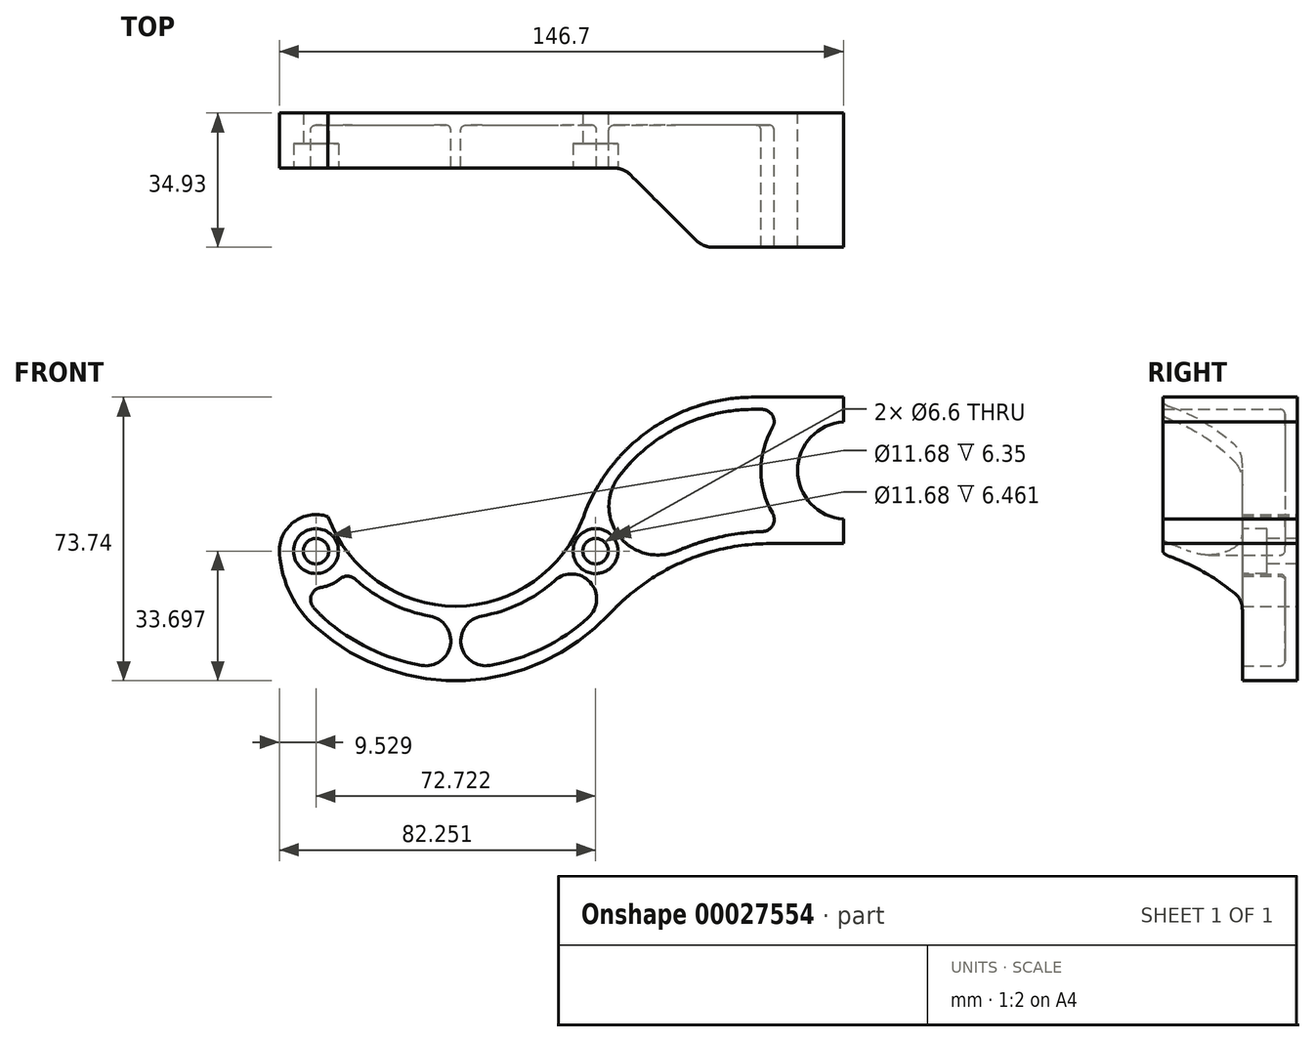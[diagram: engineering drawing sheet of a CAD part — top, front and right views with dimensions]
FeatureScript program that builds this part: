
annotation { "Feature Type Name" : "Feature", "Feature Type Description" : "" }
export const myFeature = defineFeature(function(context is Context, id is Id, definition is map)
    precondition{}
    {
        {
            var Q0;
            Q0=qCreatedBy(makeId("Front.planeOp"),FACE);
            var sketch = newSketch(context, id + "F0", { "sketchPlane" : qUnion([Q0])});
            skCircle(sketch, "E0", {"center": v(0, 0) * mm, "radius": 34.05 * mm, "construction": true});
            skLineSegment(sketch, "E1", {"start": v(0, 0) * mm, "end": v(-36.36, -21) * mm, "construction": true});
            skLineSegment(sketch, "E2", {"start": v(0, 0) * mm, "end": v(36.36, -21) * mm, "construction": true});
            skCircle(sketch, "E3.0", {"center": v(0, 0) * mm, "radius": 41.99 * mm, "construction": true});
            skCircle(sketch, "E4", {"center": v(-36.36, -21) * mm, "radius": 7.94 * mm, "construction": true});
            skCircle(sketch, "E5", {"center": v(36.36, -21) * mm, "radius": 7.94 * mm, "construction": true});
            skArc(sketch, "E6", {"start": v(-33.22, -12) * mm, "mid": v(-42.18, -13.45) * mm, "end": v(-45.86, -21.75) * mm});
            skArc(sketch, "E7.0", {"start": v(-33.22, -12) * mm, "mid": v(0, -35.32) * mm, "end": v(33.22, -12) * mm});
            skArc(sketch, "E8", {"start": v(100.8, 12.68) * mm, "mid": v(88.9, 0) * mm, "end": v(100.8, -12.68) * mm});
            skLineSegment(sketch, "E9", {"start": v(101.6, 19.05) * mm, "end": v(101.6, -19.05) * mm, "construction": true});
            skLineSegment(sketch, "E10", {"start": v(100.8, 19.05) * mm, "end": v(100.8, 12.68) * mm});
            skLineSegment(sketch, "E11.trimOffspring", {"start": v(100.8, -12.68) * mm, "end": v(100.8, -19.05) * mm});
            skLineSegment(sketch, "E12", {"start": v(100.8, 19.05) * mm, "end": v(77.45, 19.05) * mm});
            skArc(sketch, "E13", {"start": v(77.45, 19.05) * mm, "mid": v(50.43, 10.51) * mm, "end": v(33.22, -12) * mm});
            skArc(sketch, "E14.0", {"start": v(-36.36, -40.85) * mm, "mid": v(2.59, -54.62) * mm, "end": v(40.06, -37.22) * mm});
            skLineSegment(sketch, "E15", {"start": v(100.8, -19.05) * mm, "end": v(81.76, -19.05) * mm});
            skArc(sketch, "E16", {"start": v(81.76, -19.05) * mm, "mid": v(59.01, -23.8) * mm, "end": v(40.06, -37.22) * mm});
            skArc(sketch, "E17", {"start": v(-45.86, -21.75) * mm, "mid": v(-42.96, -32.22) * mm, "end": v(-36.36, -40.85) * mm});
            skLineSegment(sketch, "E18", {"start": v(-36.36, -21) * mm, "end": v(-36.36, -40.85) * mm, "construction": true});
            skLineSegment(sketch, "E19", {"start": v(-33.22, -12) * mm, "end": v(33.22, -12) * mm, "construction": true});
            skSolve(sketch);
        }
        {
            var Q0;
            Q0 = qSketchRegion(id + "F0", true);
            extrude(context, id + "F1", {"entities" : qUnion([Q0]), "depth" : 34.92 * mm});
        }
        {
            var Q0;
            Q0=makeQuery(id+"F1.opExtrude","SWEPT_FACE",FACE,{"disambiguationData":[OSD([sQuery(id+"F0.wireOp",EDGE,"E12")])]});
            var sketch = newSketch(context, id + "F2", { "sketchPlane" : qUnion([Q0])});
            skLineSegment(sketch, "E20", {"start": v(41.03, -14.29) * mm, "end": v(-45.89, -14.29) * mm});
            skLineSegment(sketch, "E21", {"start": v(-45.89, -34.93) * mm, "end": v(-45.89, -14.29) * mm});
            skLineSegment(sketch, "E22", {"start": v(43.66, -14.29) * mm, "end": v(43.66, -44.84) * mm, "construction": true});
            skLineSegment(sketch, "E23", {"start": v(45.52, -16.15) * mm, "end": v(62.43, -33.07) * mm});
            skLineSegment(sketch, "E24", {"start": v(66.92, -34.93) * mm, "end": v(100.8, -34.93) * mm});
            skLineSegment(sketch, "E25", {"start": v(100.8, -34.93) * mm, "end": v(100.8, -38.1) * mm});
            skLineSegment(sketch, "E26", {"start": v(100.8, -38.1) * mm, "end": v(-45.89, -38.1) * mm});
            skLineSegment(sketch, "E27", {"start": v(-45.89, -38.1) * mm, "end": v(-45.89, -34.93) * mm});
            skPoint(sketch, "E28.visualSharp", {"position": v(43.66, -14.29) * mm});
            skArc(sketch, "E28.filletArc", {"start": v(45.52, -16.15) * mm, "mid": v(43.46, -14.77) * mm, "end": v(41.03, -14.29) * mm});
            skPoint(sketch, "E29.visualSharp", {"position": v(64.3, -34.92) * mm});
            skArc(sketch, "E29.filletArc", {"start": v(62.43, -33.07) * mm, "mid": v(64.5, -34.44) * mm, "end": v(66.92, -34.93) * mm});
            skSolve(sketch);
        }
        {
            var Q0;
            Q0 = qSketchRegion(id + "F2", true);
            extrude(context, id + "F3", {"entities" : qUnion([Q0]), "operationType" : NewBodyOperationType.REMOVE, "endBound" : BoundingType.THROUGH_ALL, "oppositeDirection" : true, "depth" : 25.4 * mm});
        }
        {
            var Q0;
            Q0=qCreatedBy(makeId("Front.planeOp"),FACE);
            cPlane(context, id + "F4", {"entities" : qUnion([Q0]), "cplaneType" : CPlaneType.OFFSET, "offset" : 3.17 * mm, "width" : 152.4 * mm, "height" : 152.4 * mm});
        }
        {
            var Q0;
            Q0=qCreatedBy(id+"F4.planeOp",FACE);
            var sketch = newSketch(context, id + "F5", { "sketchPlane" : qUnion([Q0])});
            skArc(sketch, "E30.0", {"start": v(-26.03, -28.36) * mm, "mid": v(-17.04, -34.52) * mm, "end": v(-6.68, -37.9) * mm});
            skArc(sketch, "E31.0", {"start": v(-34.25, -38.48) * mm, "mid": v(-22.45, -46.36) * mm, "end": v(-8.94, -50.73) * mm});
            skArc(sketch, "E32", {"start": v(-35.02, -30.42) * mm, "mid": v(-32.47, -29.69) * mm, "end": v(-30.22, -28.27) * mm});
            skArc(sketch, "E33.0", {"start": v(-37.03, -35.58) * mm, "mid": v(-35.7, -37.08) * mm, "end": v(-34.25, -38.48) * mm});
            skArc(sketch, "E34.filletArc", {"start": v(-26.03, -28.36) * mm, "mid": v(-28.1, -27.53) * mm, "end": v(-30.22, -28.27) * mm});
            skArc(sketch, "E35.filletArc", {"start": v(-35.02, -30.42) * mm, "mid": v(-37.53, -32.41) * mm, "end": v(-37.03, -35.58) * mm});
            skLineSegment(sketch, "E36", {"start": v(0, 0) * mm, "end": v(-11.59, -65.71) * mm, "construction": true});
            skLineSegment(sketch, "E37", {"start": v(0, 0) * mm, "end": v(11.66, -66.14) * mm, "construction": true});
            skArc(sketch, "E38", {"start": v(-8.94, -50.73) * mm, "mid": v(-1.4, -45.45) * mm, "end": v(-6.68, -37.9) * mm});
            skArc(sketch, "E39", {"start": v(6.68, -37.9) * mm, "mid": v(1.4, -45.45) * mm, "end": v(8.94, -50.73) * mm});
            skLineSegment(sketch, "E40", {"start": v(0, 0) * mm, "end": v(47.81, -53.1) * mm, "construction": true});
            skArc(sketch, "E41", {"start": v(34.47, -38.28) * mm, "mid": v(34.95, -29.09) * mm, "end": v(25.76, -28.6) * mm});
            skArc(sketch, "E42.trimOffspring", {"start": v(6.68, -37.9) * mm, "mid": v(16.87, -34.6) * mm, "end": v(25.76, -28.6) * mm});
            skArc(sketch, "E43.trimOffspring", {"start": v(8.94, -50.73) * mm, "mid": v(22.58, -46.3) * mm, "end": v(34.47, -38.28) * mm});
            skArc(sketch, "E44.0", {"start": v(77.45, 15.87) * mm, "mid": v(57.79, 11.22) * mm, "end": v(42.3, -1.76) * mm});
            skArc(sketch, "E45.0", {"start": v(79.73, -15.9) * mm, "mid": v(68.43, -17.37) * mm, "end": v(57.61, -20.94) * mm});
            skArc(sketch, "E46.0", {"start": v(82.35, 11.11) * mm, "mid": v(79.38, -0.02) * mm, "end": v(82.37, -11.14) * mm});
            skLineSegment(sketch, "E47.0", {"start": v(79.6, 15.87) * mm, "end": v(72.44, 15.87) * mm});
            skArc(sketch, "E48.filletArc", {"start": v(79.73, -15.9) * mm, "mid": v(82.4, -14.27) * mm, "end": v(82.37, -11.14) * mm});
            skArc(sketch, "E49.filletArc", {"start": v(82.35, 11.11) * mm, "mid": v(82.35, 14.29) * mm, "end": v(79.6, 15.87) * mm});
            skLineSegment(sketch, "E50", {"start": v(81.76, -75.96) * mm, "end": v(33.25, 15.26) * mm, "construction": true});
            skLineSegment(sketch, "E51", {"start": v(81.76, -75.96) * mm, "end": v(81.76, 37.95) * mm, "construction": true});
            skArc(sketch, "E52", {"start": v(42.3, -1.76) * mm, "mid": v(42.58, -17.23) * mm, "end": v(57.61, -20.94) * mm});
            skSolve(sketch);
        }
        {
            var Q0;
            Q0 = qSketchRegion(id + "F5", true);
            extrude(context, id + "F6", {"entities" : qUnion([Q0]), "operationType" : NewBodyOperationType.REMOVE, "depth" : 38.1 * mm});
        }
        {
            var Q0;
            Q0=makeQuery(id+"F6.boolean.opBoolean","COPY",EDGE,{"derivedFrom":makeQuery(id+"F6.opExtrude","CAP_EDGE",EDGE,{"disambiguationData":[OSD([sQuery(id+"F5.wireOp",EDGE,"E30.0")])],"isStart":true})});
            var Q1;
            Q1=makeQuery(id+"F6.boolean.opBoolean","COPY",EDGE,{"derivedFrom":makeQuery(id+"F6.opExtrude","CAP_EDGE",EDGE,{"disambiguationData":[OSD([sQuery(id+"F5.wireOp",EDGE,"E42.trimOffspring")])],"isStart":true})});
            var Q2;
            Q2=makeQuery(id+"F6.boolean.opBoolean","COPY",EDGE,{"derivedFrom":makeQuery(id+"F6.opExtrude","CAP_EDGE",EDGE,{"disambiguationData":[OSD([sQuery(id+"F5.wireOp",EDGE,"E44.0")])],"isStart":true})});
            fillet(context, id + "F7", {"entities" : qUnion([Q0, Q1, Q2]), "radius" : 1.27 * mm, "tangentPropagation" : true, "allowEdgeOverflow" : false});
        }
        {
            var Q0;
            Q0=makeQuery(id+"F3.boolean.opBoolean","COPY",FACE,{"derivedFrom":makeQuery(id+"F3.opExtrude","SWEPT_FACE",FACE,{"disambiguationData":[OSD([sQuery(id+"F2.wireOp",EDGE,"E20")])]})});
            var sketch = newSketch(context, id + "F8", { "sketchPlane" : qUnion([Q0])});
            skCircle(sketch, "E53", {"center": v(-36.36, -21) * mm, "radius": 3.3 * mm});
            skCircle(sketch, "E54", {"center": v(36.36, -21) * mm, "radius": 3.3 * mm});
            skSolve(sketch);
        }
        {
            var Q0;
            Q0 = qSketchRegion(id + "F8", true);
            extrude(context, id + "F9", {"entities" : qUnion([Q0]), "operationType" : NewBodyOperationType.REMOVE, "endBound" : BoundingType.THROUGH_ALL, "oppositeDirection" : true, "depth" : 25.4 * mm});
        }
        {
            var Q0;
            Q0=makeQuery(id+"F3.boolean.opBoolean","COPY",FACE,{"derivedFrom":makeQuery(id+"F3.opExtrude","SWEPT_FACE",FACE,{"disambiguationData":[OSD([sQuery(id+"F2.wireOp",EDGE,"E20")])]})});
            var sketch = newSketch(context, id + "F10", { "sketchPlane" : qUnion([Q0])});
            skCircle(sketch, "E55", {"center": v(-36.36, -21) * mm, "radius": 5.84 * mm});
            skCircle(sketch, "E56", {"center": v(36.36, -21) * mm, "radius": 5.84 * mm});
            skSolve(sketch);
        }
        {
            var Q0;
            Q0 = qSketchRegion(id + "F10", true);
            extrude(context, id + "F11", {"entities" : qUnion([Q0]), "operationType" : NewBodyOperationType.REMOVE, "oppositeDirection" : true, "depth" : 6.35 * mm, "hasSecondDirection" : true, "secondDirectionOppositeDirection" : false, "secondDirectionDepth" : 3.17 * mm});
        }
    });
